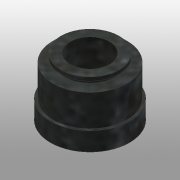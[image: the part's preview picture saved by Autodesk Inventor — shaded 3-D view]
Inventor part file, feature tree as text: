
AUTODESK INVENTOR PART (.ipt)
format: ipt  version: 2016 (Build 200138000, 138)  size: 153,088 bytes
history: native  units: mm
features: revolve x2, sketch x2, projected_geometry x1
ambient origin geometry x8: Origin, YZ Plane, XZ Plane, XY Plane, X Axis, Y Axis, Z Axis, Center Point
bodies: Solid1 (feature_tree)
feature tree (5):
  revolve  "Revolution1"  [1 undecoded]
  revolve  "Revolution2"  [1 undecoded]
  sketch  "Sketch1"  dims[d0=5.0mm d1=10.4mm]
  sketch  "Sketch3"  dims[d2=1.0mm d3=0.0mm d4=3.0mm d5=7.41mm d6=1.7mm d8=6.0mm d9=6.408039mm d10=3.2mm d11=90.0deg d13=0.6mm d14=1.3mm d15=4.15mm d16=4.75mm d17=90.0deg]
  projected_geometry  "Project Cut Edges1"
note: 2 required parameter values undecoded (feature->parameter linkage not recoverable at this tier; creation-order binding heuristic only, values carry confidence <= 0.55)
